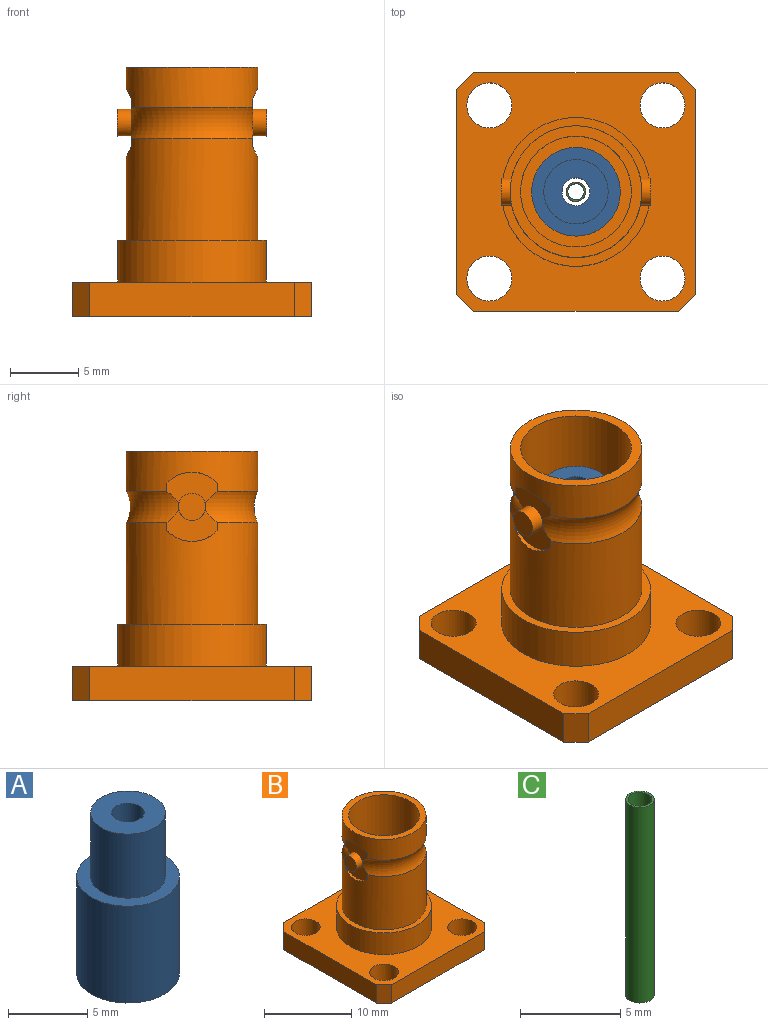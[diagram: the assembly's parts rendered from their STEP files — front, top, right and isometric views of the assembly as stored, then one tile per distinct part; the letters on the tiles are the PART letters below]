
ASSEMBLY  parts=3 mates=2
PART A: 6 faces, bbox 6.5x6.5x12.4 mm
  f0: cylinder r=1.02mm len=12.45mm, axis (0,0,-1), area 80.1mm2, adj f1,f5
  f1: plane 6.5x6.5mm, normal (0,0,-1), area 29.9mm2, adj f0,f2
  f2: cylinder r=3.25mm len=7.49mm, axis (0,0,-1), area 153.1mm2, adj f1,f3
  f3: plane 6.5x6.5mm, normal (0,0,1), area 15.7mm2, adj f2,f4
  f4: cylinder r=2.36mm len=4.95mm, axis (0,0,-1), area 73.5mm2, adj f3,f5
  f5: plane 4.72x4.72mm, normal (0,0,1), area 14.2mm2, adj f0,f4
PART B: 38 faces, bbox 17.5x17.5x18.3 mm
  f0: torus R=7.09mm, axis (0,0,-1), area 28.4mm2, adj f2,f3,f26,f28,f31,f32,f35,f37
  f1: torus R=7.09mm, axis (0,0,-1), area 28.4mm2, adj f2,f3,f26,f28,f31,f32,f35,f37
  f2: cylinder r=4.83mm len=9.65mm, axis (0,0,-1), area 218.5mm2, adj f0,f1,f25,f34,f35,f36,f37
  f3: cylinder r=4.83mm len=9.65mm, axis (0,0,-1), area 79.9mm2, adj f0,f1,f20,f30,f31,f32,f33
  f4: plane 6.5x6.5mm, normal (0,0,1), area 4.3mm2, adj f8,f23
  f5: plane 14.99x2.54mm, normal (0,1,0), area 38.1mm2, adj f10,f11,f12,f15
  f6: plane 14.99x2.54mm, normal (-1,0,0), area 38.1mm2, adj f10,f11,f14,f15
  f7: plane 14.99x2.54mm, normal (0,-1,0), area 38.1mm2, adj f10,f11,f13,f14
  f8: cylinder r=3.03mm len=6.06mm, axis (0,0,1), area 48.4mm2, adj f4,f10
  f9: plane 14.99x2.54mm, normal (1,0,0), area 38.1mm2, adj f10,f11,f12,f13
  f10: plane 17.53x17.53mm, normal (0,0,-1), area 240.8mm2, adj f5,f6,f7,f8,f9,f12,f13,f14
  f11: plane 17.53x17.53mm, normal (0,0,1), area 176mm2, adj f5,f6,f7,f9,f12,f13,f14,f15
  f12: plane 2.54x1.27mm, normal (0.71,0.71,0), area 4.6mm2, adj f5,f9,f10,f11
  f13: plane 2.54x1.27mm, normal (0.71,-0.71,0), area 4.6mm2, adj f7,f9,f10,f11
  f14: plane 2.54x1.27mm, normal (-0.71,-0.71,0), area 4.6mm2, adj f6,f7,f10,f11
  f15: plane 2.54x1.27mm, normal (-0.71,0.71,0), area 4.6mm2, adj f5,f6,f10,f11
  f16: cylinder r=1.65mm len=3.3mm, axis (0,0,1), area 26.3mm2, adj f10,f11
  f17: cylinder r=1.65mm len=3.3mm, axis (0,0,1), area 26.3mm2, adj f10,f11
  f18: cylinder r=1.65mm len=3.3mm, axis (0,0,1), area 26.3mm2, adj f10,f11
  f19: cylinder r=1.65mm len=3.3mm, axis (0,0,1), area 26.3mm2, adj f10,f11
  f20: plane 9.65x9.65mm, normal (0,0,1), area 21.3mm2, adj f3,f21
  f21: cylinder r=4.06mm len=8.41mm, axis (0,0,-1), area 214.7mm2, adj f20,f22
  f22: plane 8.13x8.13mm, normal (0,0,1), area 18.7mm2, adj f21,f23
  f23: cylinder r=3.25mm len=7.34mm, axis (0,0,-1), area 150mm2, adj f4,f22
  f24: cylinder r=5.46mm len=10.92mm, axis (0,0,-1), area 104.6mm2, adj f11,f25
  f25: plane 10.92x10.92mm, normal (0,0,1), area 20.5mm2, adj f2,f24
  f26: cylinder r=0.99mm len=1.98mm, axis (-1,0,0), area 6.4mm2, adj f0,f1,f27,f31,f35
  f27: plane 1.98x1.98mm, normal (1,0,0), area 3.1mm2, adj f26
  f28: cylinder r=0.99mm len=1.98mm, axis (-1,0,0), area 6.4mm2, adj f0,f1,f29,f32,f37
  f29: plane 1.98x1.98mm, normal (-1,0,0), area 3.1mm2, adj f28
  f30: cylinder r=2.54mm len=3.7mm, axis (1,0,0), area 1mm2, adj f3,f31
  f31: plane 3.7x2.34mm, normal (1,0,0), area 5.6mm2, adj f0,f1,f3,f26,f30
  f32: plane 3.7x2.34mm, normal (-1,0,0), area 5.6mm2, adj f0,f1,f3,f28,f33
  f33: cylinder r=2.54mm len=3.7mm, axis (1,0,0), area 1mm2, adj f3,f32
  f34: cylinder r=2.54mm len=3.7mm, axis (1,0,0), area 1mm2, adj f2,f35
  f35: plane 3.7x2.34mm, normal (1,0,0), area 5.6mm2, adj f0,f1,f2,f26,f34
  f36: cylinder r=2.54mm len=3.7mm, axis (1,0,0), area 1mm2, adj f2,f37
  f37: plane 3.7x2.34mm, normal (-1,0,0), area 5.6mm2, adj f0,f1,f2,f28,f36
PART C: 4 faces, bbox 1.4x1.4x11.9 mm
  f0: cylinder r=0.6mm len=11.94mm, axis (0,0,-1), area 44.7mm2, adj f1,f3
  f1: plane 1.42x1.42mm, normal (0,0,-1), area 0.5mm2, adj f0,f2
  f2: cylinder r=0.71mm len=11.94mm, axis (0,0,-1), area 53.3mm2, adj f1,f3
  f3: plane 1.42x1.42mm, normal (0,0,1), area 0.5mm2, adj f0,f2
PLACE A at identity
PLACE B at identity fixed
PLACE C at identity
MATE fastened A.f0 <-> B.f8  axis (0,0,-1) through (0,0,0)mm
MATE fastened C.f0 <-> A.f0  axis (0,0,-1) through (0,0,0)mm
